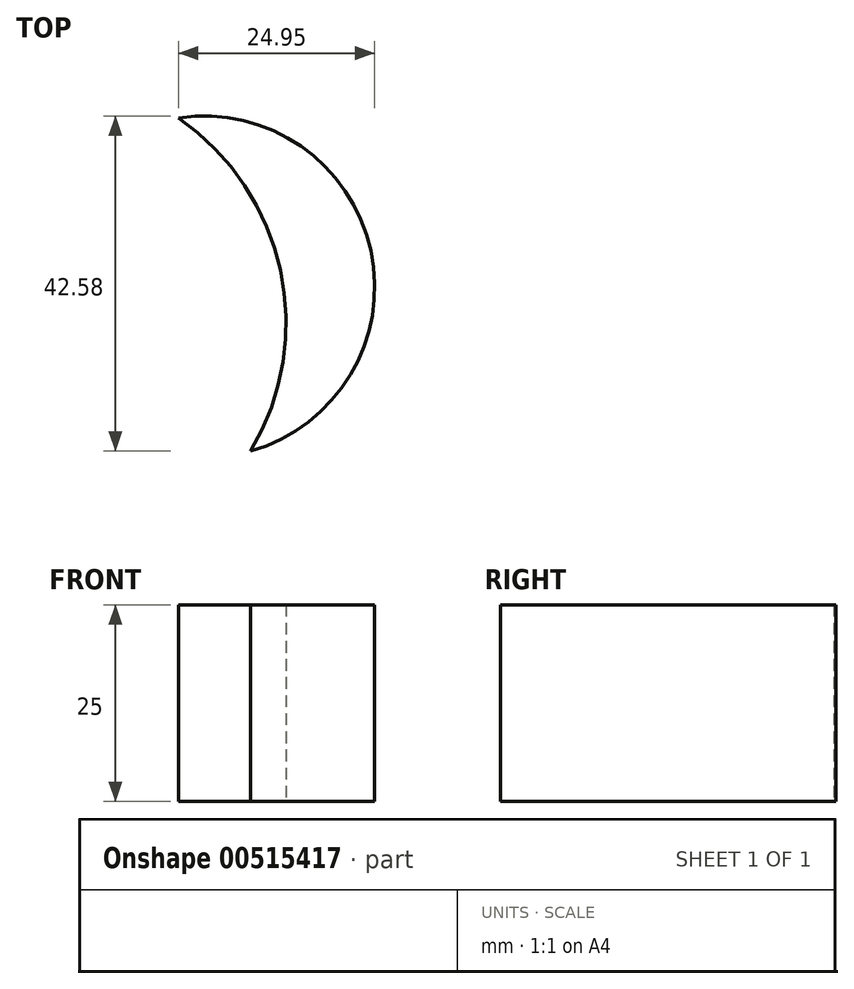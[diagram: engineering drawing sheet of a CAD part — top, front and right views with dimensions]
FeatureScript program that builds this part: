
annotation { "Feature Type Name" : "Feature", "Feature Type Description" : "" }
export const myFeature = defineFeature(function(context is Context, id is Id, definition is map)
    precondition{}
    {
        {
            var Q0;
            Q0=qCreatedBy(makeId("Top.planeOp"),FACE);
            var sketch = newSketch(context, id + "F0", { "sketchPlane" : qUnion([Q0])});
            skArc(sketch, "E0", {"start": v(34.67, -32.88) * mm, "mid": v(49.94, -7.4) * mm, "end": v(25.5, 9.46) * mm});
            skArc(sketch, "E1", {"start": v(34.67, -32.88) * mm, "mid": v(38.46, -9.9) * mm, "end": v(25.5, 9.46) * mm});
            skSolve(sketch);
        }
        {
            var Q0;
            Q0 = qSketchRegion(id + "F0", true);
            extrude(context, id + "F1", {"entities" : qUnion([Q0]), "depth" : 25 * mm, "offsetDistance" : 25 * mm});
        }
    });
